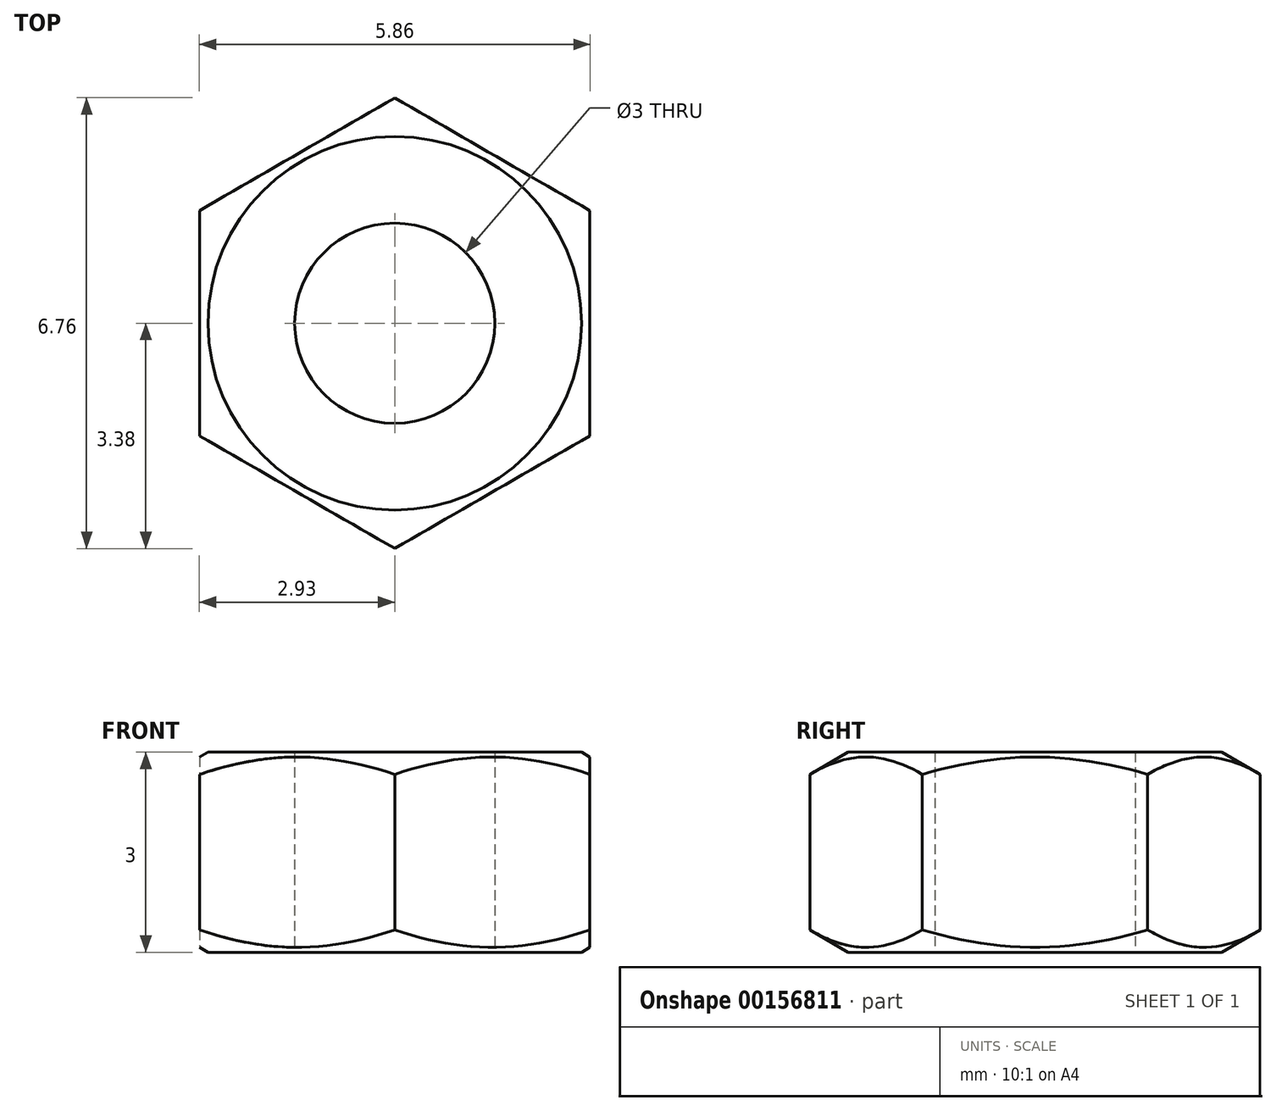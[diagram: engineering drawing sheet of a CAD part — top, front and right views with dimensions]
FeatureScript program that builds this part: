
annotation { "Feature Type Name" : "Feature", "Feature Type Description" : "" }
export const myFeature = defineFeature(function(context is Context, id is Id, definition is map)
    precondition{}
    {
        {
            var Q0;
            Q0=qCreatedBy(makeId("Top.planeOp"),FACE);
            var sketch = newSketch(context, id + "F0", { "sketchPlane" : qUnion([Q0])});
            skCircle(sketch, "E0.cCircle", {"center": v(0, 0) * mm, "radius": 2.93 * mm, "construction": true});
            skLineSegment(sketch, "E0.0", {"start": v(2.93, 1.69) * mm, "end": v(2.93, -1.69) * mm});
            skLineSegment(sketch, "E0.1", {"start": v(2.92, -1.69) * mm, "end": v(0, -3.38) * mm});
            skLineSegment(sketch, "E0.2", {"start": v(0, -3.38) * mm, "end": v(-2.92, -1.69) * mm});
            skLineSegment(sketch, "E0.3", {"start": v(-2.93, -1.69) * mm, "end": v(-2.93, 1.69) * mm});
            skLineSegment(sketch, "E0.4", {"start": v(-2.93, 1.69) * mm, "end": v(0, 3.38) * mm});
            skLineSegment(sketch, "E0.5", {"start": v(0, 3.38) * mm, "end": v(2.92, 1.69) * mm});
            skPoint(sketch, "E0.0.midPoint", {"position": v(2.93, 0) * mm});
            skCircle(sketch, "E1", {"center": v(0, 0) * mm, "radius": 1.5 * mm});
            skSolve(sketch);
        }
        {
            var Q0;
            Q0=qSketchRegion(id+"F0",true);
            extrude(context, id + "F1", {"entities" : qUnion([Q0]), "depth" : 3 * mm});
        }
        {
            var Q0;
            Q0=qCreatedBy(makeId("Front.planeOp"),FACE);
            var sketch = newSketch(context, id + "F2", { "sketchPlane" : qUnion([Q0])});
            skLineSegment(sketch, "E2", {"start": v(0, 0) * mm, "end": v(0, 3) * mm, "construction": true});
            skLineSegment(sketch, "E3", {"start": v(0, 1.5) * mm, "end": v(2.92, 1.5) * mm, "construction": true});
            skPoint(sketch, "E3.endSnap0", {"position": v(0, 1.5) * mm});
            skLineSegment(sketch, "E4", {"start": v(2.8, 3) * mm, "end": v(4.88, 3) * mm});
            skLineSegment(sketch, "E5", {"start": v(4.88, 3) * mm, "end": v(4.88, 1.8) * mm});
            skLineSegment(sketch, "E6", {"start": v(4.88, 1.8) * mm, "end": v(2.8, 3) * mm});
            skLineSegment(sketch, "E7.MirrorCS", {"start": v(4.88, 0) * mm, "end": v(4.88, 1.2) * mm});
            skLineSegment(sketch, "E8.MirrorCS", {"start": v(2.8, 0) * mm, "end": v(4.88, 0) * mm});
            skLineSegment(sketch, "E9.MirrorCS", {"start": v(4.88, 1.2) * mm, "end": v(2.8, 0) * mm});
            skSolve(sketch);
        }
        {
            var Q0;
            Q0=qSketchRegion(id+"F2",true);
            var Q1;
            Q1=sQuery(id+"F2.wireOp",EDGE,"E2");
            revolve(context, id + "F3", {"operationType" : NewBodyOperationType.REMOVE, "entities" : qUnion([Q0]), "axis" : qUnion([Q1]), "revolveType" : RevolveType.FULL});
        }
    });
